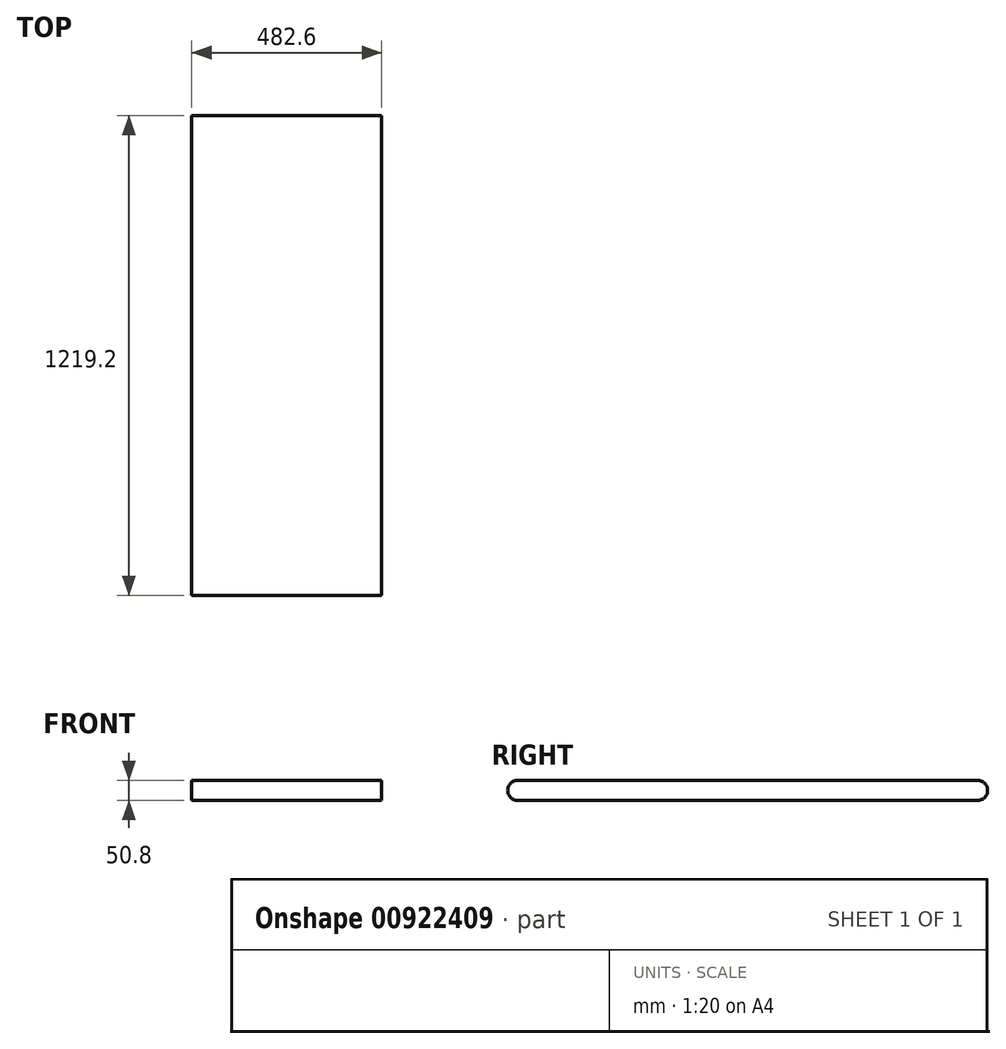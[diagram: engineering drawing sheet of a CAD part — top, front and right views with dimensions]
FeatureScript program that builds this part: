
annotation { "Feature Type Name" : "Feature", "Feature Type Description" : "" }
export const myFeature = defineFeature(function(context is Context, id is Id, definition is map)
    precondition{}
    {
        {
            var Q0;
            Q0=qCreatedBy(makeId("Right.planeOp"),FACE);
            var sketch = newSketch(context, id + "F0", { "sketchPlane" : qUnion([Q0])});
            skLineSegment(sketch, "E0.bottom", {"start": v(609.6, 25.4) * mm, "end": v(-609.6, 25.4) * mm});
            skLineSegment(sketch, "E0.top", {"start": v(609.6, -25.4) * mm, "end": v(-609.6, -25.4) * mm});
            skLineSegment(sketch, "E0.left", {"start": v(609.6, 25.4) * mm, "end": v(609.6, -25.4) * mm});
            skLineSegment(sketch, "E0.right", {"start": v(-609.6, 25.4) * mm, "end": v(-609.6, -25.4) * mm});
            skPoint(sketch, "E0.middle", {"position": v(0, 0) * mm});
            skSolve(sketch);
        }
        {
            var Q0;
            Q0=makeQuery(id+"F0.imprint","IMPRINT",FACE,{"disambiguationData":[TD([[makeQuery(id+"F0.imprint","IMPRINT",EDGE,{"derivedFrom":sQuery(id+"F0.wireOp",EDGE,"E0.bottom")}),1.0]])]});
            extrude(context, id + "F1", {"entities" : qUnion([Q0]), "depth" : 482.6 * mm, "offsetDistance" : 25.4 * mm, "symmetric" : true});
        }
        {
            var Q0;
            Q0=makeQuery(id+"F1.opExtrude","SWEPT_EDGE",EDGE,{"disambiguationData":[OSD([sQuery(id+"F0.wireOp",EDGE,"E0.bottom"),sQuery(id+"F0.wireOp",EDGE,"E0.right")])]});
            var Q1;
            Q1=makeQuery(id+"F1.opExtrude","SWEPT_EDGE",EDGE,{"disambiguationData":[OSD([sQuery(id+"F0.wireOp",EDGE,"E0.top"),sQuery(id+"F0.wireOp",EDGE,"E0.right")])]});
            var Q2;
            Q2=makeQuery(id+"F1.opExtrude","SWEPT_EDGE",EDGE,{"disambiguationData":[OSD([sQuery(id+"F0.wireOp",EDGE,"E0.top"),sQuery(id+"F0.wireOp",EDGE,"E0.left")])]});
            var Q3;
            Q3=makeQuery(id+"F1.opExtrude","SWEPT_EDGE",EDGE,{"disambiguationData":[OSD([sQuery(id+"F0.wireOp",EDGE,"E0.bottom"),sQuery(id+"F0.wireOp",EDGE,"E0.left")])]});
            fillet(context, id + "F2", {"entities" : qUnion([Q0, Q1, Q2, Q3]), "radius" : 25.4 * mm, "tangentPropagation" : true, "allowEdgeOverflow" : false});
        }
    });
